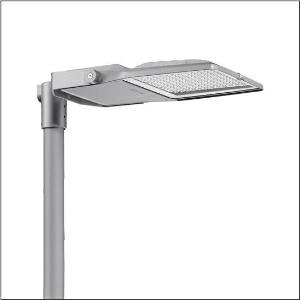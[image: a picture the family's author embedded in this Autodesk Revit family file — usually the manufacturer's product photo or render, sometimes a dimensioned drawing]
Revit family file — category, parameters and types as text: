
# Revit family: floodlight_fl_21_iq_midi___pl64_5xa7781e2e3a_93f0
name_source: partatom
category: Lighting Fixtures
units: mm (PartAtom-declared; Revit-internal decimal feet)

## family parameters
Cut with Voids When Loaded = No
Host = Face
Light Source = No
Part Type = Normal
Room Calculation Point = No
Round Connector Dimension = Use Diameter
Shared = No

## types (1)
- --- (1 x LED, 25930 lm, 208.1 W, 3000K)
    Apparent Load = 208 VA
    CIE Flux Codes = 28 80 98 100 100
    Color Rendering = 70
    Color Temperature = 3000K
    Default Elevation = 1800 mm
    Description = Floodlight FL 21 iQ midi, floodlight, primary light control with lens, of PMMA, primary optical cover: protective disc, of toughened safety glass, transparent, light distribution: PL64, light emission: direct distribution, installation type: surface-mounted, LED, High Power LED, rated luminous flux: 25.930lm, luminous efficacy: 125lm/W, light colour: 730, colour temperature: 3000K, control gear: ECG iQ, control: optimised constant luminous flux control (CLO 2.0), Desk-Remote (wireless, voltage-free reading and setting of iQ features in the workshop via application-optimized NFC function/RFID function), Light-Fading, Smart-Wire, Night-Set, Lumen-Switch, Temp-Guard, Auto-Match, with terminal, 6-pole, mains connection: 220..240V, AC, 50/60Hz, start of lifetime: 208W, end of service life: 227W, reduction: 90W, luminaire housing, of diecast aluminium, powder-coated, Siteco® metallic grey (DB 702S), corrosivity category C5 mid according to DIN EN ISO 12944, sealing non-destructively replaceable, please order mast flange separately, mast bracket, of steel, galvanised, powder-coated, Siteco® metallic grey (DB 702S), protection rating (complete): IP66, insulation class (complete): insulation class II (safety insulation), certification: CE, protection symbol: D, impact resistance: IK08, permissible operating ambient temperature: -40..+40°C, permissible operating ambient temperature for outdoor applications: -40..+50°C, standard: DIN EN 12944, LABS conformity tested according to VDMA 24364:2018-05, packaging unit: 1 piece

Light Distribution: PL64
    Height = 76 mm
    Lamp = 1 x LED
    Lamp Light Flux = 25930 lm
    Lamp Power = 208.1 W
    Lamp count = 1
    Length = 657 mm
    Luminous efficacy = 125 lm/W
    Manufacturer = Siteco
    ModVariant = No
    Model = 5XA7781E2E3A
    Number of Poles = 1
    OnlyDefault = Yes
    Power Factor = 1
    Product Name = Floodlight FL 21 iQ midi | PL64
    Product group = floodlight | pylon annexe
    ProductGroupID = 6200
    Protection Class = Protection class II
    Protection Degree = IP 66
    RLX_Detail_Level = 1
    RLX_Emergency_Light_Flux = 0 lm
    RLX_Emergency_Type = 0
    RLX_Emergency_Type_DB = No
    RlxData = <blob elided: 153461 chars, md5=bceeadf3>
    Socket = socket
    Standby Power = 0 W
    System Light Flux = 25930 lm
    System Power = 208 W
    Type Comments = factory setting: luminous flux: 100 % | dim-lin: 254 | 710 mA
    Type Image = l_1007123.jpg
    URL = http://relux.com
    VarID = @adj_037413
    Voltage = 0 V
    Weight = 0.00 kg
    Width = 442 mm

## geometry (parser evidence)
native form markers: Blend x4, Sweep x12
no freeform markers — native parametric forms only
